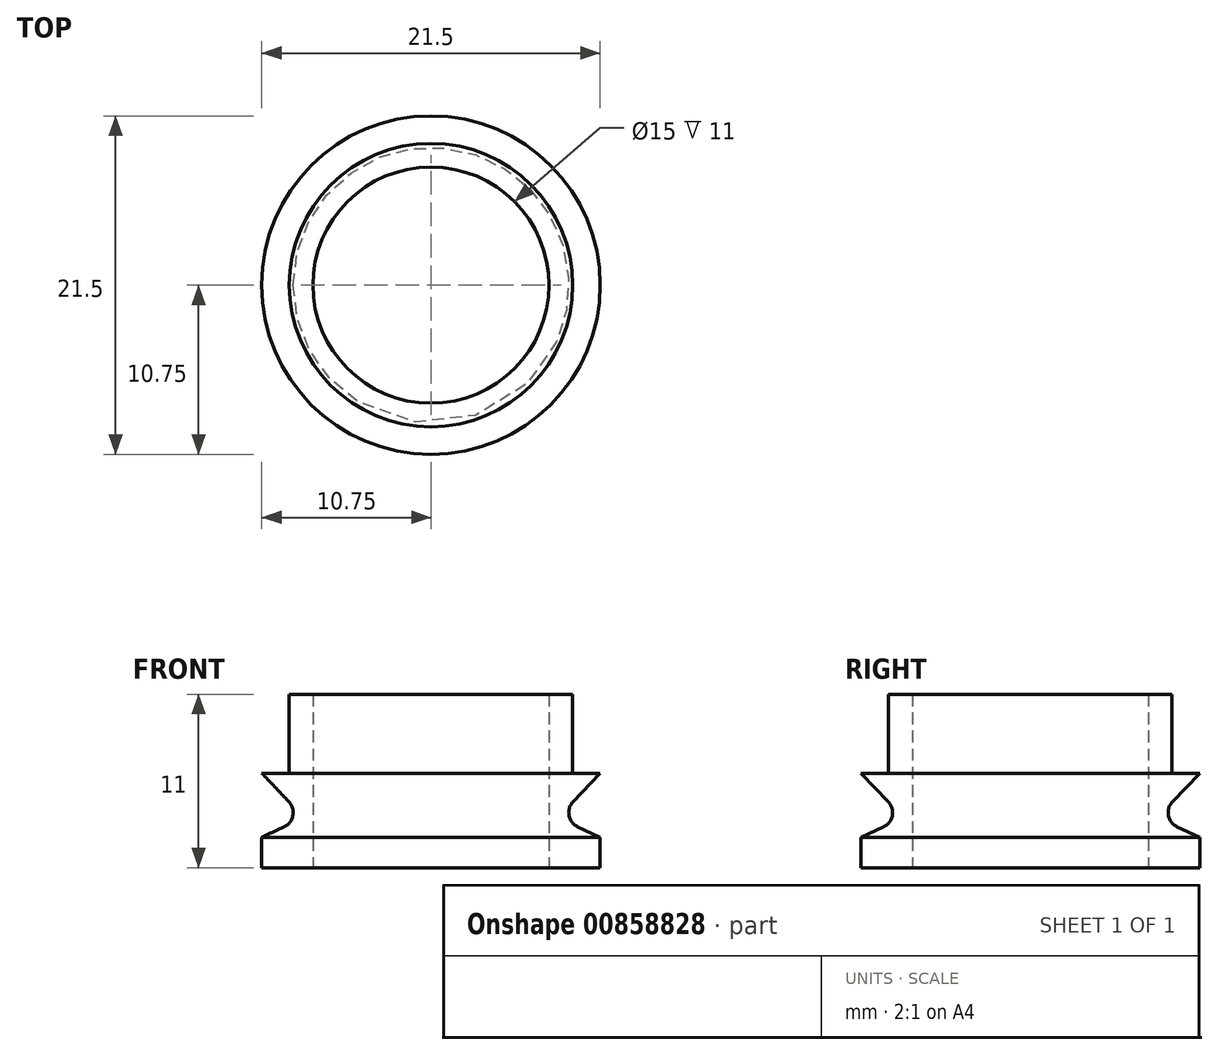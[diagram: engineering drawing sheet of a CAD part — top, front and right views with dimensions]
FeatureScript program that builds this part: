
annotation { "Feature Type Name" : "Feature", "Feature Type Description" : "" }
export const myFeature = defineFeature(function(context is Context, id is Id, definition is map)
    precondition{}
    {
        {
            var Q0;
            Q0=qCreatedBy(makeId("Front.planeOp"),FACE);
            var sketch = newSketch(context, id + "F0", { "sketchPlane" : qUnion([Q0])});
            skLineSegment(sketch, "E0", {"start": v(0, 0) * mm, "end": v(0, 27.07) * mm, "construction": true});
            skLineSegment(sketch, "E1", {"start": v(0, 0) * mm, "end": v(-7.5, 0) * mm, "construction": true});
            skLineSegment(sketch, "E2", {"start": v(-7.5, 0) * mm, "end": v(-10.75, 0) * mm});
            skLineSegment(sketch, "E3", {"start": v(-7.5, 0) * mm, "end": v(-7.5, 11) * mm});
            skLineSegment(sketch, "E4", {"start": v(-7.5, 11) * mm, "end": v(-9, 11) * mm});
            skLineSegment(sketch, "E5", {"start": v(-9, 11) * mm, "end": v(-9, 6) * mm});
            skLineSegment(sketch, "E6", {"start": v(-9, 6) * mm, "end": v(-10.75, 6) * mm});
            skLineSegment(sketch, "E7", {"start": v(-10.75, 6) * mm, "end": v(-10.75, 3.5) * mm, "construction": true});
            skLineSegment(sketch, "E8", {"start": v(-10.75, 3.5) * mm, "end": v(-9.75, 3.5) * mm, "construction": true});
            skLineSegment(sketch, "E9", {"start": v(-10.75, 6) * mm, "end": v(-9.03, 4.19) * mm});
            skLineSegment(sketch, "E10", {"start": v(-10.75, 3.5) * mm, "end": v(-10.75, 0) * mm, "construction": true});
            skLineSegment(sketch, "E11", {"start": v(-9.75, 3.5) * mm, "end": v(-10.75, 3.03) * mm, "construction": true});
            skLineSegment(sketch, "E12", {"start": v(-10.14, 2.22) * mm, "end": v(-10.75, 1.93) * mm, "construction": true});
            skLineSegment(sketch, "E13", {"start": v(-10.75, 1.93) * mm, "end": v(-9.32, 2.6) * mm});
            skLineSegment(sketch, "E14", {"start": v(-10.75, 0) * mm, "end": v(-10.75, 1.93) * mm});
            skArc(sketch, "E15", {"start": v(-9.32, 2.6) * mm, "mid": v(-8.77, 3.32) * mm, "end": v(-9.03, 4.19) * mm});
            skSolve(sketch);
        }
        {
            var Q0;
            Q0=makeQuery(id+"F0.imprint","IMPRINT",FACE,{"disambiguationData":[TD([[makeQuery(id+"F0.imprint","IMPRINT",EDGE,{"derivedFrom":sQuery(id+"F0.wireOp",EDGE,"E2")}),-1.0]])]});
            var Q1;
            Q1=sQuery(id+"F0.wireOp",EDGE,"E0");
            revolve(context, id + "F1", {"surfaceOperationType" : NewSurfaceOperationType.NEW, "entities" : qUnion([Q0]), "axis" : qUnion([Q1]), "revolveType" : RevolveType.FULL});
        }
    });
